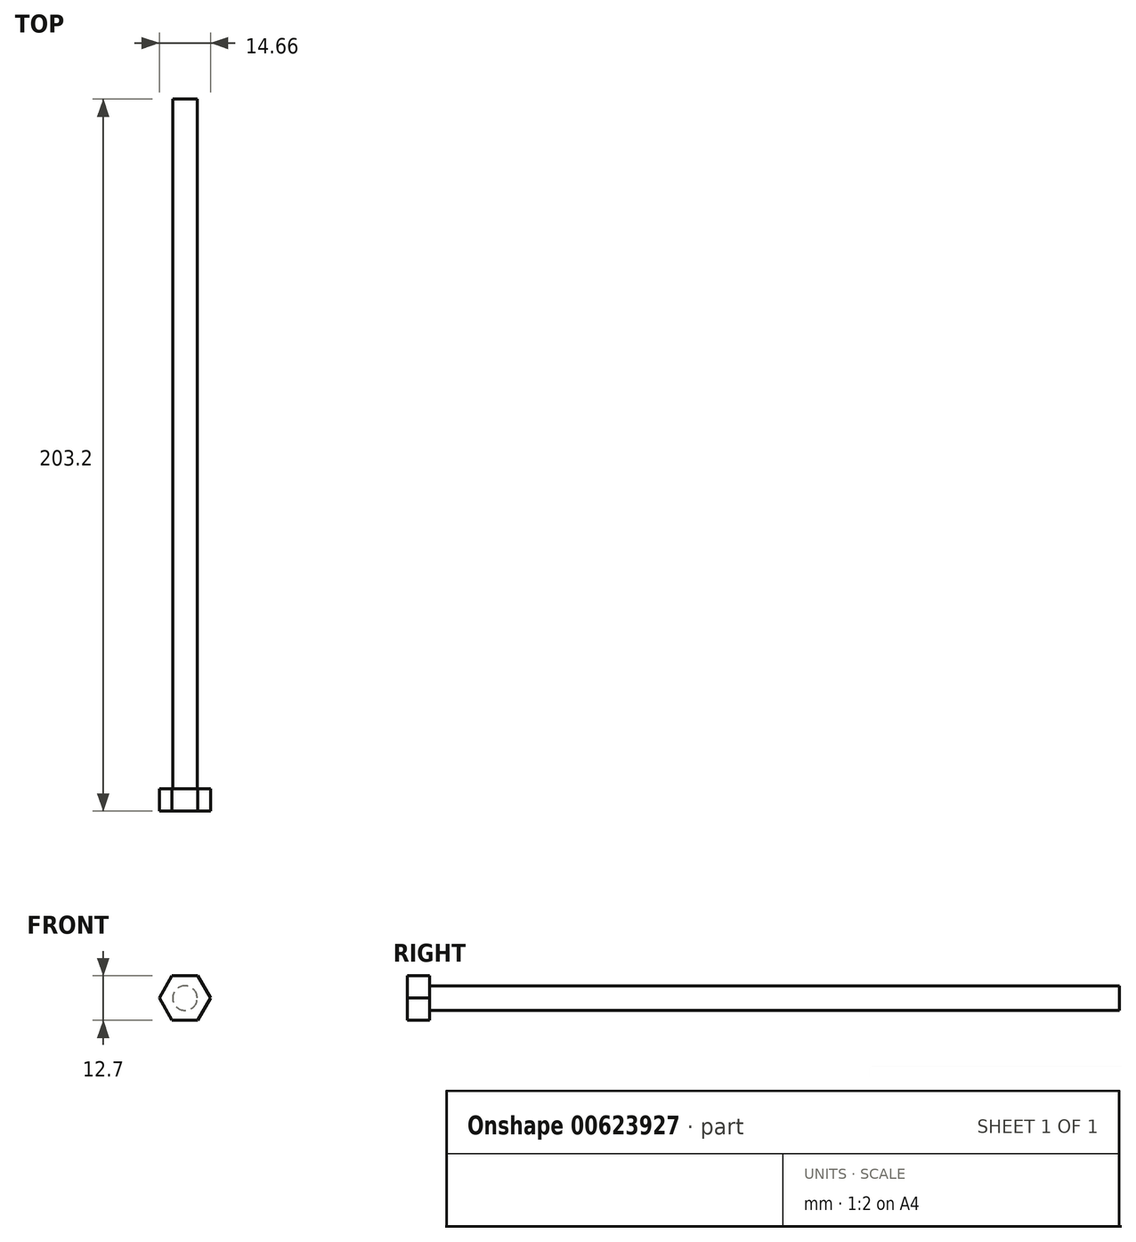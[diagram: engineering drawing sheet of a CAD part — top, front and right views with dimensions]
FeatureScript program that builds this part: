
annotation { "Feature Type Name" : "Feature", "Feature Type Description" : "" }
export const myFeature = defineFeature(function(context is Context, id is Id, definition is map)
    precondition{}
    {
        {
            var Q0;
            Q0=qCreatedBy(makeId("Front.planeOp"),FACE);
            var sketch = newSketch(context, id + "F0", { "sketchPlane" : qUnion([Q0])});
            skCircle(sketch, "E0", {"center": v(0, 0) * mm, "radius": 3.5 * mm});
            skSolve(sketch);
        }
        {
            var Q0;
            Q0=qSketchRegion(id+"F0",true);
            extrude(context, id + "F1", {"entities" : qUnion([Q0]), "depth" : 203.2 * mm, "offsetDistance" : 25.4 * mm});
        }
        {
            var Q0;
            Q0=makeQuery(id+"F1.opExtrude","CAP_FACE",FACE,{"disambiguationData":[OSD([sQuery(id+"F0.wireOp",EDGE,"E0")])],"isStart":false});
            var sketch = newSketch(context, id + "F2", { "sketchPlane" : qUnion([Q0])});
            skCircle(sketch, "E1.cCircle", {"center": v(0, 0) * mm, "radius": 6.35 * mm, "construction": true});
            skLineSegment(sketch, "E1.0", {"start": v(3.67, 6.35) * mm, "end": v(7.33, 0) * mm});
            skLineSegment(sketch, "E1.1", {"start": v(7.33, 0) * mm, "end": v(3.67, -6.35) * mm});
            skLineSegment(sketch, "E1.2", {"start": v(3.67, -6.35) * mm, "end": v(-3.67, -6.35) * mm});
            skLineSegment(sketch, "E1.3", {"start": v(-3.67, -6.35) * mm, "end": v(-7.33, 0) * mm});
            skLineSegment(sketch, "E1.4", {"start": v(-7.33, 0) * mm, "end": v(-3.67, 6.35) * mm});
            skLineSegment(sketch, "E1.5", {"start": v(-3.67, 6.35) * mm, "end": v(3.67, 6.35) * mm});
            skPoint(sketch, "E1.0.midPoint", {"position": v(5.5, 3.17) * mm});
            skSolve(sketch);
        }
        {
            var Q0;
            Q0=qSketchRegion(id+"F2",true);
            extrude(context, id + "F3", {"entities" : qUnion([Q0]), "operationType" : NewBodyOperationType.ADD, "oppositeDirection" : true, "depth" : 6.35 * mm, "offsetDistance" : 25.4 * mm});
        }
    });
